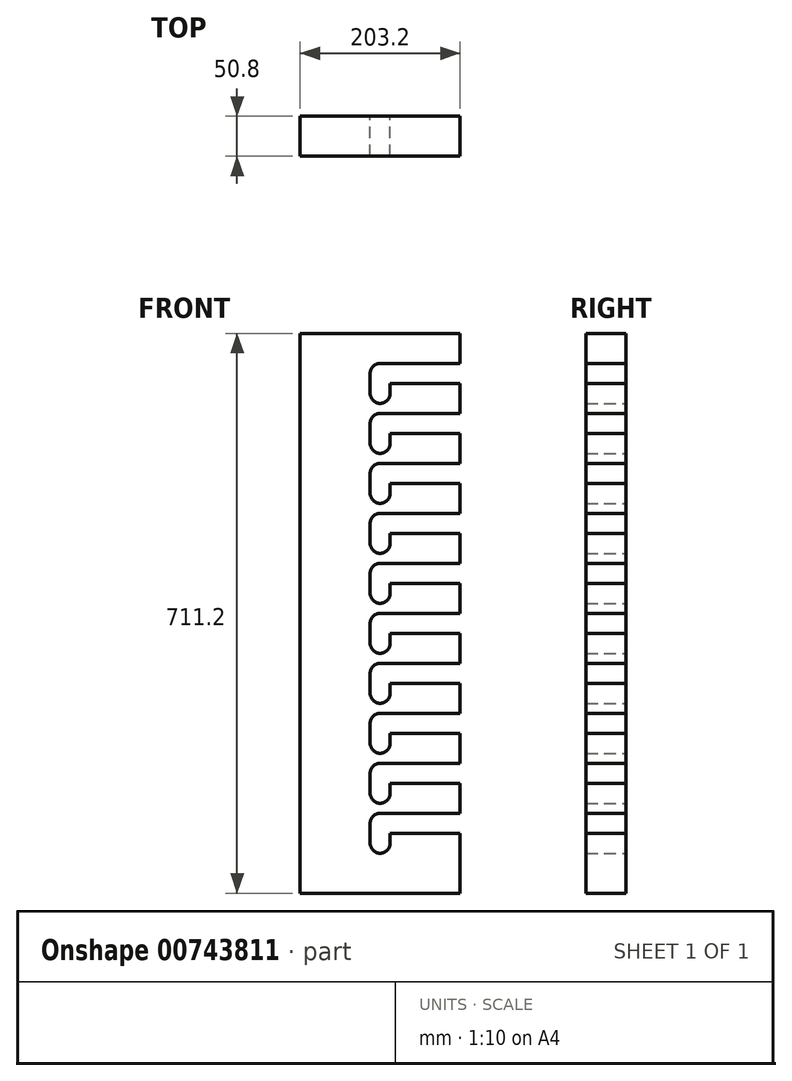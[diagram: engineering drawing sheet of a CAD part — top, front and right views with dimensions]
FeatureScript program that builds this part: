
annotation { "Feature Type Name" : "Feature", "Feature Type Description" : "" }
export const myFeature = defineFeature(function(context is Context, id is Id, definition is map)
    precondition{}
    {
        {
            var Q0;
            Q0=qCreatedBy(makeId("Front.planeOp"),FACE);
            var sketch = newSketch(context, id + "F0", { "sketchPlane" : qUnion([Q0])});
            skLineSegment(sketch, "E0.bottom", {"start": v(101.6, 355.6) * mm, "end": v(-101.6, 355.6) * mm});
            skLineSegment(sketch, "E0.top", {"start": v(101.6, -355.6) * mm, "end": v(-101.6, -355.6) * mm});
            skLineSegment(sketch, "E0.left", {"start": v(101.6, 355.6) * mm, "end": v(101.6, -355.6) * mm});
            skLineSegment(sketch, "E0.right", {"start": v(-101.6, 355.6) * mm, "end": v(-101.6, -355.6) * mm});
            skPoint(sketch, "E0.middle", {"position": v(0, 0) * mm});
            skLineSegment(sketch, "E1", {"start": v(12.7, 292.1) * mm, "end": v(101.6, 292.1) * mm});
            skCircle(sketch, "E2", {"center": v(0, 279.4) * mm, "radius": 12.7 * mm});
            skLineSegment(sketch, "E3", {"start": v(12.7, 292.1) * mm, "end": v(12.7, 279.4) * mm});
            skLineSegment(sketch, "E4", {"start": v(101.6, 317.5) * mm, "end": v(0, 317.5) * mm});
            skCircle(sketch, "E5", {"center": v(0, 304.8) * mm, "radius": 12.7 * mm});
            skLineSegment(sketch, "E6", {"start": v(-12.7, 304.8) * mm, "end": v(-12.7, 279.4) * mm});
            skLineSegment(sketch, "E7.0.1.0", {"start": v(101.6, 254) * mm, "end": v(0, 254) * mm});
            skLineSegment(sketch, "E7.0.1.1", {"start": v(-12.7, 241.3) * mm, "end": v(-12.7, 215.9) * mm});
            skCircle(sketch, "E7.0.1.2", {"center": v(0, 241.3) * mm, "radius": 12.7 * mm});
            skLineSegment(sketch, "E7.0.1.3", {"start": v(12.7, 228.6) * mm, "end": v(101.6, 228.6) * mm});
            skCircle(sketch, "E7.0.1.4", {"center": v(0, 215.9) * mm, "radius": 12.7 * mm});
            skLineSegment(sketch, "E7.0.1.5", {"start": v(12.7, 228.6) * mm, "end": v(12.7, 215.9) * mm});
            skLineSegment(sketch, "E7.0.2.0", {"start": v(101.6, 190.5) * mm, "end": v(0, 190.5) * mm});
            skLineSegment(sketch, "E7.0.2.1", {"start": v(-12.7, 177.8) * mm, "end": v(-12.7, 152.4) * mm});
            skCircle(sketch, "E7.0.2.2", {"center": v(0, 177.8) * mm, "radius": 12.7 * mm});
            skLineSegment(sketch, "E7.0.2.3", {"start": v(12.7, 165.1) * mm, "end": v(101.6, 165.1) * mm});
            skCircle(sketch, "E7.0.2.4", {"center": v(0, 152.4) * mm, "radius": 12.7 * mm});
            skLineSegment(sketch, "E7.0.2.5", {"start": v(12.7, 165.1) * mm, "end": v(12.7, 152.4) * mm});
            skLineSegment(sketch, "E7.0.3.0", {"start": v(101.6, 127) * mm, "end": v(0, 127) * mm});
            skLineSegment(sketch, "E7.0.3.1", {"start": v(-12.7, 114.3) * mm, "end": v(-12.7, 88.9) * mm});
            skCircle(sketch, "E7.0.3.2", {"center": v(0, 114.3) * mm, "radius": 12.7 * mm});
            skLineSegment(sketch, "E7.0.3.3", {"start": v(12.7, 101.6) * mm, "end": v(101.6, 101.6) * mm});
            skCircle(sketch, "E7.0.3.4", {"center": v(0, 88.9) * mm, "radius": 12.7 * mm});
            skLineSegment(sketch, "E7.0.3.5", {"start": v(12.7, 101.6) * mm, "end": v(12.7, 88.9) * mm});
            skLineSegment(sketch, "E7.0.4.0", {"start": v(101.6, 63.5) * mm, "end": v(0, 63.5) * mm});
            skLineSegment(sketch, "E7.0.4.1", {"start": v(-12.7, 50.8) * mm, "end": v(-12.7, 25.4) * mm});
            skCircle(sketch, "E7.0.4.2", {"center": v(0, 50.8) * mm, "radius": 12.7 * mm});
            skLineSegment(sketch, "E7.0.4.3", {"start": v(12.7, 38.1) * mm, "end": v(101.6, 38.1) * mm});
            skCircle(sketch, "E7.0.4.4", {"center": v(0, 25.4) * mm, "radius": 12.7 * mm});
            skLineSegment(sketch, "E7.0.4.5", {"start": v(12.7, 38.1) * mm, "end": v(12.7, 25.4) * mm});
            skLineSegment(sketch, "E7.0.5.0", {"start": v(101.6, 0) * mm, "end": v(0, 0) * mm});
            skLineSegment(sketch, "E7.0.5.1", {"start": v(-12.7, -12.7) * mm, "end": v(-12.7, -38.1) * mm});
            skCircle(sketch, "E7.0.5.2", {"center": v(0, -12.7) * mm, "radius": 12.7 * mm});
            skLineSegment(sketch, "E7.0.5.3", {"start": v(12.7, -25.4) * mm, "end": v(101.6, -25.4) * mm});
            skCircle(sketch, "E7.0.5.4", {"center": v(0, -38.1) * mm, "radius": 12.7 * mm});
            skLineSegment(sketch, "E7.0.5.5", {"start": v(12.7, -25.4) * mm, "end": v(12.7, -38.1) * mm});
            skLineSegment(sketch, "E7.0.6.0", {"start": v(101.6, -63.5) * mm, "end": v(0, -63.5) * mm});
            skLineSegment(sketch, "E7.0.6.1", {"start": v(-12.7, -76.2) * mm, "end": v(-12.7, -101.6) * mm});
            skCircle(sketch, "E7.0.6.2", {"center": v(0, -76.2) * mm, "radius": 12.7 * mm});
            skLineSegment(sketch, "E7.0.6.3", {"start": v(12.7, -88.9) * mm, "end": v(101.6, -88.9) * mm});
            skCircle(sketch, "E7.0.6.4", {"center": v(0, -101.6) * mm, "radius": 12.7 * mm});
            skLineSegment(sketch, "E7.0.6.5", {"start": v(12.7, -88.9) * mm, "end": v(12.7, -101.6) * mm});
            skLineSegment(sketch, "E7.0.7.0", {"start": v(101.6, -127) * mm, "end": v(0, -127) * mm});
            skLineSegment(sketch, "E7.0.7.1", {"start": v(-12.7, -139.7) * mm, "end": v(-12.7, -165.1) * mm});
            skCircle(sketch, "E7.0.7.2", {"center": v(0, -139.7) * mm, "radius": 12.7 * mm});
            skLineSegment(sketch, "E7.0.7.3", {"start": v(12.7, -152.4) * mm, "end": v(101.6, -152.4) * mm});
            skCircle(sketch, "E7.0.7.4", {"center": v(0, -165.1) * mm, "radius": 12.7 * mm});
            skLineSegment(sketch, "E7.0.7.5", {"start": v(12.7, -152.4) * mm, "end": v(12.7, -165.1) * mm});
            skLineSegment(sketch, "E7.0.8.0", {"start": v(101.6, -190.5) * mm, "end": v(0, -190.5) * mm});
            skLineSegment(sketch, "E7.0.8.1", {"start": v(-12.7, -203.2) * mm, "end": v(-12.7, -228.6) * mm});
            skCircle(sketch, "E7.0.8.2", {"center": v(0, -203.2) * mm, "radius": 12.7 * mm});
            skLineSegment(sketch, "E7.0.8.3", {"start": v(12.7, -215.9) * mm, "end": v(101.6, -215.9) * mm});
            skCircle(sketch, "E7.0.8.4", {"center": v(0, -228.6) * mm, "radius": 12.7 * mm});
            skLineSegment(sketch, "E7.0.8.5", {"start": v(12.7, -215.9) * mm, "end": v(12.7, -228.6) * mm});
            skLineSegment(sketch, "E7.0.9.0", {"start": v(101.6, -254) * mm, "end": v(0, -254) * mm});
            skLineSegment(sketch, "E7.0.9.1", {"start": v(-12.7, -266.7) * mm, "end": v(-12.7, -292.1) * mm});
            skCircle(sketch, "E7.0.9.2", {"center": v(0, -266.7) * mm, "radius": 12.7 * mm});
            skLineSegment(sketch, "E7.0.9.3", {"start": v(12.7, -279.4) * mm, "end": v(101.6, -279.4) * mm});
            skCircle(sketch, "E7.0.9.4", {"center": v(0, -292.1) * mm, "radius": 12.7 * mm});
            skLineSegment(sketch, "E7.0.9.5", {"start": v(12.7, -279.4) * mm, "end": v(12.7, -292.1) * mm});
            skLineSegment(sketch, "E7.direction1", {"start": v(0, 317.5) * mm, "end": v(25.4, 317.5) * mm, "construction": true});
            skLineSegment(sketch, "E7.direction2", {"start": v(0, 317.5) * mm, "end": v(0, 254) * mm, "construction": true});
            skSolve(sketch);
        }
        {
            var Q0;
            {var subQ3=sQuery(id+"F0.wireOp",EDGE,"E0.bottom");Q0=makeQuery(id+"F0.imprint","IMPRINT",FACE,{"disambiguationData":[TD([[makeQuery(id+"F0.imprint","IMPRINT",EDGE,{"derivedFrom":subQ3}),1.0]])]});}
            extrude(context, id + "F1", {"entities" : qUnion([Q0]), "depth" : 50.8 * mm, "offsetDistance" : 25.4 * mm});
        }
    });
